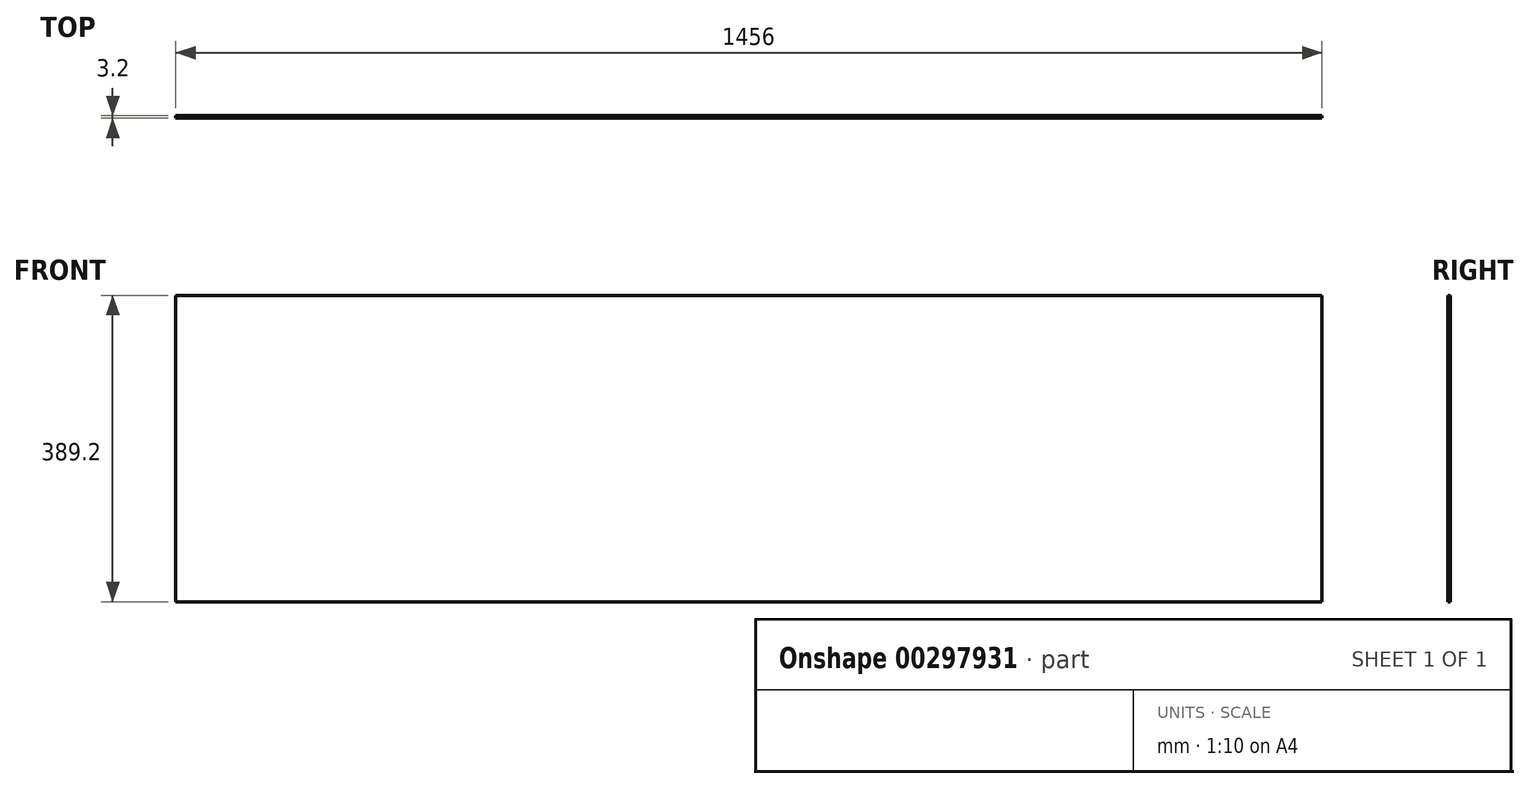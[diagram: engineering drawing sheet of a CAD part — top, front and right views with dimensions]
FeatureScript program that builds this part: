
annotation { "Feature Type Name" : "Feature", "Feature Type Description" : "" }
export const myFeature = defineFeature(function(context is Context, id is Id, definition is map)
    precondition{}
    {
        {
            var Q0;
            Q0=qCreatedBy(makeId("Front.planeOp"),FACE);
            var sketch = newSketch(context, id + "F0", { "sketchPlane" : qUnion([Q0])});
            skLineSegment(sketch, "E0.bottom", {"start": v(728, 194.6) * mm, "end": v(-728, 194.6) * mm});
            skLineSegment(sketch, "E0.top", {"start": v(728, -194.6) * mm, "end": v(-728, -194.6) * mm});
            skLineSegment(sketch, "E0.left", {"start": v(728, 194.6) * mm, "end": v(728, -194.6) * mm});
            skLineSegment(sketch, "E0.right", {"start": v(-728, 194.6) * mm, "end": v(-728, -194.6) * mm});
            skPoint(sketch, "E0.middle", {"position": v(0, 0) * mm});
            skSolve(sketch);
        }
        {
            var Q0;
            Q0=makeQuery(id+"F0.imprint","IMPRINT",FACE,{"disambiguationData":[TD([[makeQuery(id+"F0.imprint","IMPRINT",EDGE,{"derivedFrom":sQuery(id+"F0.wireOp",EDGE,"E0.bottom")}),1.0]])]});
            extrude(context, id + "F1", {"entities" : qUnion([Q0]), "endBound" : BoundingType.SYMMETRIC, "depth" : 3.2 * mm});
        }
    });
